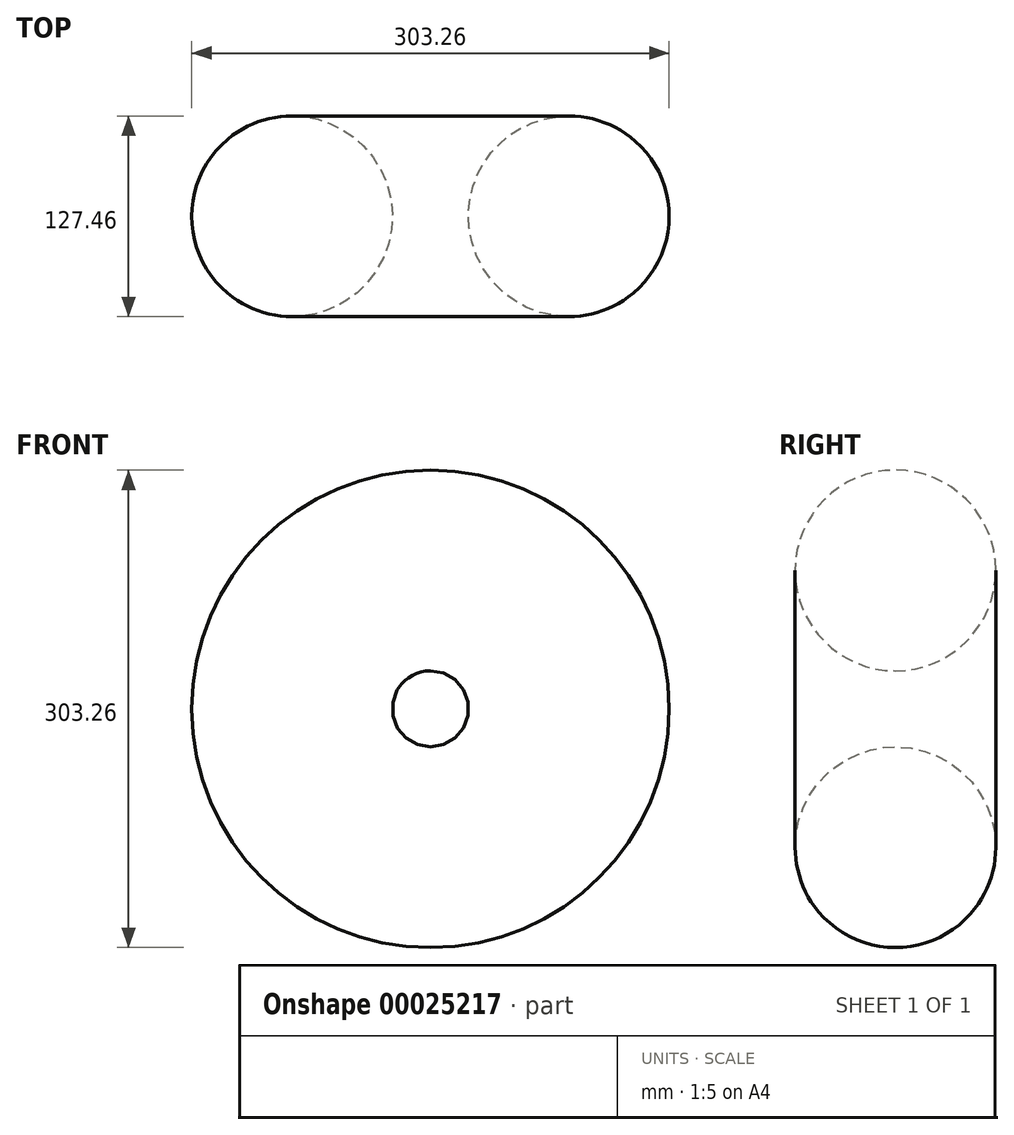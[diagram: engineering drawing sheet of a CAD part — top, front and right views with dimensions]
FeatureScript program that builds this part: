
annotation { "Feature Type Name" : "Feature", "Feature Type Description" : "" }
export const myFeature = defineFeature(function(context is Context, id is Id, definition is map)
    precondition{}
    {
        {
            var Q0;
            Q0=qCreatedBy(makeId("Top.planeOp"),FACE);
            var sketch = newSketch(context, id + "F0", { "sketchPlane" : qUnion([Q0])});
            skLineSegment(sketch, "E0", {"start": v(-81.01, 69) * mm, "end": v(-81.01, -58.47) * mm});
            skSolve(sketch);
        }
        {
            var Q0;
            Q0=qCreatedBy(makeId("Top.planeOp"),FACE);
            var sketch = newSketch(context, id + "F1", { "sketchPlane" : qUnion([Q0])});
            skCircle(sketch, "E1", {"center": v(6.89, 0) * mm, "radius": 63.73 * mm});
            skSolve(sketch);
        }
        {
            var Q0;
            Q0 = qSketchRegion(id + "F1", true);
            var Q1;
            Q1=sQuery(id+"F0.wireOp",EDGE,"E0");
            revolve(context, id + "F2", {"entities" : qUnion([Q0]), "axis" : qUnion([Q1]), "revolveType" : RevolveType.FULL});
        }
    });
